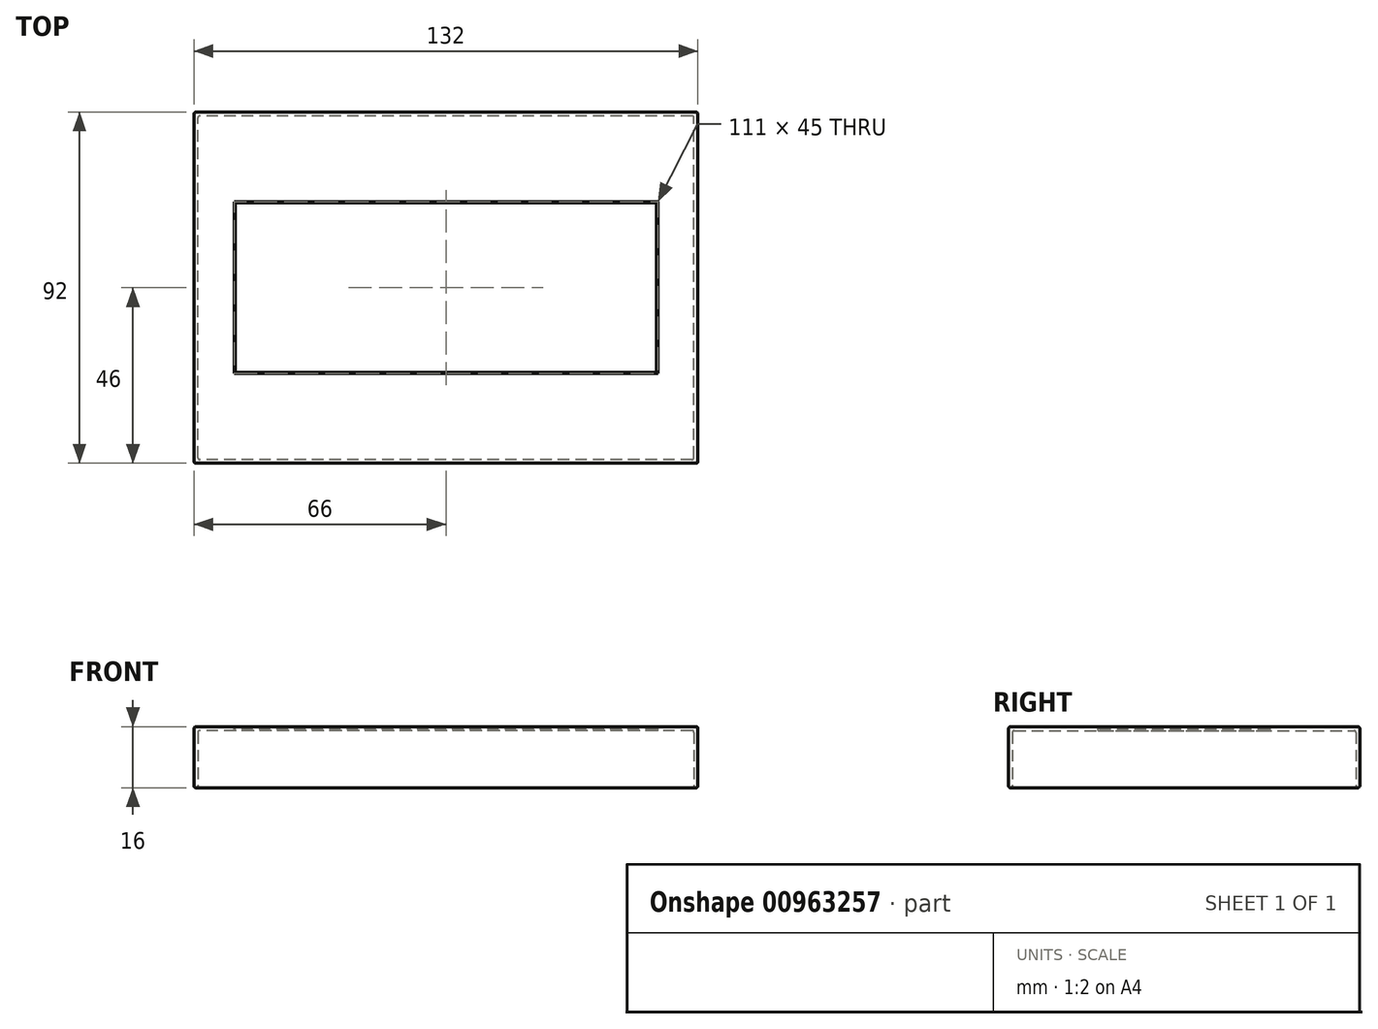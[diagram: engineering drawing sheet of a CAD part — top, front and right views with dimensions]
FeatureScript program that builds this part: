
annotation { "Feature Type Name" : "Feature", "Feature Type Description" : "" }
export const myFeature = defineFeature(function(context is Context, id is Id, definition is map)
    precondition{}
    {
        {
            var Q0;
            Q0=qCreatedBy(makeId("Top.planeOp"),FACE);
            var sketch = newSketch(context, id + "F0", { "sketchPlane" : qUnion([Q0])});
            skLineSegment(sketch, "E0.bottom", {"start": v(66, -46) * mm, "end": v(-66, -46) * mm});
            skLineSegment(sketch, "E0.top", {"start": v(66, 46) * mm, "end": v(-66, 46) * mm});
            skLineSegment(sketch, "E0.left", {"start": v(66, -46) * mm, "end": v(66, 46) * mm});
            skLineSegment(sketch, "E0.right", {"start": v(-66, -46) * mm, "end": v(-66, 46) * mm});
            skPoint(sketch, "E0.middle", {"position": v(0, 0) * mm});
            skSolve(sketch);
        }
        {
            var Q0;
            Q0 = qSketchRegion(id + "F0", true);
            extrude(context, id + "F1", {"entities" : qUnion([Q0]), "depth" : 16 * mm, "offsetDistance" : 25 * mm});
        }
        {
            var Q0;
            Q0=makeQuery(id+"F1.opExtrude","CAP_FACE",FACE,{"disambiguationData":[OSD([sQuery(id+"F0.wireOp",EDGE,"E0.bottom"),sQuery(id+"F0.wireOp",EDGE,"E0.top"),sQuery(id+"F0.wireOp",EDGE,"E0.left"),sQuery(id+"F0.wireOp",EDGE,"E0.right")])],"isStart":true});
            shell(context, id + "F2", {"entities" : qUnion([Q0]), "thickness" : 1 * mm});
        }
        {
            var Q0;
            Q0=makeQuery(id+"F1.opExtrude","SWEPT_EDGE",EDGE,{"disambiguationData":[OSD([sQuery(id+"F0.wireOp",EDGE,"E0.bottom"),sQuery(id+"F0.wireOp",EDGE,"E0.left")])]});
            var Q1;
            Q1=makeQuery(id+"F1.opExtrude","SWEPT_FACE",FACE,{"disambiguationData":[OSD([sQuery(id+"F0.wireOp",EDGE,"E0.bottom")])]});
            var Q2;
            Q2=makeQuery(id+"F1.opExtrude","SWEPT_EDGE",EDGE,{"disambiguationData":[OSD([sQuery(id+"F0.wireOp",EDGE,"E0.bottom"),sQuery(id+"F0.wireOp",EDGE,"E0.right")])]});
            var Q3;
            Q3=makeQuery(id+"F1.opExtrude","SWEPT_EDGE",EDGE,{"disambiguationData":[OSD([sQuery(id+"F0.wireOp",EDGE,"E0.top"),sQuery(id+"F0.wireOp",EDGE,"E0.left")])]});
            var Q4;
            Q4=makeQuery(id+"F1.opExtrude","CAP_FACE",FACE,{"disambiguationData":[OSD([sQuery(id+"F0.wireOp",EDGE,"E0.bottom"),sQuery(id+"F0.wireOp",EDGE,"E0.top"),sQuery(id+"F0.wireOp",EDGE,"E0.left"),sQuery(id+"F0.wireOp",EDGE,"E0.right")])],"isStart":false});
            var Q5;
            Q5=makeQuery(id+"F1.opExtrude","SWEPT_EDGE",EDGE,{"disambiguationData":[OSD([sQuery(id+"F0.wireOp",EDGE,"E0.top"),sQuery(id+"F0.wireOp",EDGE,"E0.right")])]});
            var Q6;
            Q6=makeQuery(id+"F1.opExtrude","SWEPT_FACE",FACE,{"disambiguationData":[OSD([sQuery(id+"F0.wireOp",EDGE,"E0.top")])]});
            var Q7;
            Q7=makeQuery(id+"F1.opExtrude","CAP_EDGE",EDGE,{"disambiguationData":[OSD([sQuery(id+"F0.wireOp",EDGE,"E0.bottom")])],"isStart":true});
            var Q8;
            Q8=makeQuery(id+"F1.opExtrude","SWEPT_FACE",FACE,{"disambiguationData":[OSD([sQuery(id+"F0.wireOp",EDGE,"E0.left")])]});
            var Q9;
            Q9=makeQuery(id+"F1.opExtrude","CAP_EDGE",EDGE,{"disambiguationData":[OSD([sQuery(id+"F0.wireOp",EDGE,"E0.bottom")])],"isStart":false});
            var Q10;
            Q10=makeQuery(id+"F1.opExtrude","SWEPT_FACE",FACE,{"disambiguationData":[OSD([sQuery(id+"F0.wireOp",EDGE,"E0.right")])]});
            var Q11;
            Q11=makeQuery(id+"F1.opExtrude","CAP_EDGE",EDGE,{"disambiguationData":[OSD([sQuery(id+"F0.wireOp",EDGE,"E0.top")])],"isStart":true});
            var Q12;
            Q12=makeQuery(id+"F1.opExtrude","CAP_EDGE",EDGE,{"disambiguationData":[OSD([sQuery(id+"F0.wireOp",EDGE,"E0.left")])],"isStart":true});
            var Q13;
            Q13=makeQuery(id+"F1.opExtrude","CAP_EDGE",EDGE,{"disambiguationData":[OSD([sQuery(id+"F0.wireOp",EDGE,"E0.right")])],"isStart":true});
            var Q14;
            Q14=makeQuery(id+"F1.opExtrude","CAP_EDGE",EDGE,{"disambiguationData":[OSD([sQuery(id+"F0.wireOp",EDGE,"E0.right")])],"isStart":false});
            var Q15;
            Q15=makeQuery(id+"F2.opShell","OFFSET_FACE",FACE,{"disambiguationData":[OSD([sQuery(id+"F0.wireOp",EDGE,"E0.bottom")])]});
            var Q16;
            Q16=makeQuery(id+"F2.opShell","OFFSET_FACE",FACE,{"disambiguationData":[OSD([sQuery(id+"F0.wireOp",EDGE,"E0.bottom"),sQuery(id+"F0.wireOp",EDGE,"E0.top"),sQuery(id+"F0.wireOp",EDGE,"E0.left"),sQuery(id+"F0.wireOp",EDGE,"E0.right")])]});
            var Q17;
            Q17=makeQuery(id+"F2.opShell","OFFSET_EDGE",EDGE,{"disambiguationData":[OSD([sQuery(id+"F0.wireOp",EDGE,"E0.top"),sQuery(id+"F0.wireOp",EDGE,"E0.left")])]});
            var Q18;
            Q18=makeQuery(id+"F2.opShell","OFFSET_FACE",FACE,{"disambiguationData":[OSD([sQuery(id+"F0.wireOp",EDGE,"E0.top")])]});
            var Q19;
            Q19=makeQuery(id+"F2.opShell","OFFSET_EDGE",EDGE,{"disambiguationData":[OSD([sQuery(id+"F0.wireOp",EDGE,"E0.top"),sQuery(id+"F0.wireOp",EDGE,"E0.right")])]});
            var Q20;
            Q20=makeQuery(id+"F2.opShell","OFFSET_FACE",FACE,{"disambiguationData":[OSD([sQuery(id+"F0.wireOp",EDGE,"E0.left")])]});
            var Q21;
            {var subQ0=sQuery(id+"F0.wireOp",EDGE,"E0.bottom");Q21=makeQuery(id+"F2.opShell","OFFSET_EDGE",EDGE,{"disambiguationData":[OSD([subQ0]),TDD([makeQuery(id+"F1.opExtrude","CAP_EDGE",EDGE,{"disambiguationData":[OSD([subQ0])],"isStart":true})])]});}
            var Q22;
            Q22=makeQuery(id+"F2.opShell","OFFSET_FACE",FACE,{"disambiguationData":[OSD([sQuery(id+"F0.wireOp",EDGE,"E0.right")])]});
            var Q23;
            Q23=makeQuery(id+"F1.opExtrude","CAP_FACE",FACE,{"disambiguationData":[OSD([sQuery(id+"F0.wireOp",EDGE,"E0.bottom"),sQuery(id+"F0.wireOp",EDGE,"E0.top"),sQuery(id+"F0.wireOp",EDGE,"E0.left"),sQuery(id+"F0.wireOp",EDGE,"E0.right")])],"isStart":true});
            var Q24;
            {var subQ0=sQuery(id+"F0.wireOp",EDGE,"E0.top");Q24=makeQuery(id+"F2.opShell","OFFSET_EDGE",EDGE,{"disambiguationData":[OSD([subQ0]),TDD([makeQuery(id+"F1.opExtrude","CAP_EDGE",EDGE,{"disambiguationData":[OSD([subQ0])],"isStart":true})])]});}
            var Q25;
            {var subQ0=sQuery(id+"F0.wireOp",EDGE,"E0.top");Q25=makeQuery(id+"F2.opShell","OFFSET_EDGE",EDGE,{"disambiguationData":[OSD([subQ0]),TDD([makeQuery(id+"F1.opExtrude","CAP_EDGE",EDGE,{"disambiguationData":[OSD([subQ0])],"isStart":false})])]});}
            var Q26;
            {var subQ0=sQuery(id+"F0.wireOp",EDGE,"E0.left");Q26=makeQuery(id+"F2.opShell","OFFSET_EDGE",EDGE,{"disambiguationData":[OSD([subQ0]),TDD([makeQuery(id+"F1.opExtrude","CAP_EDGE",EDGE,{"disambiguationData":[OSD([subQ0])],"isStart":true})])]});}
            var Q27;
            {var subQ0=sQuery(id+"F0.wireOp",EDGE,"E0.left");Q27=makeQuery(id+"F2.opShell","OFFSET_EDGE",EDGE,{"disambiguationData":[OSD([subQ0]),TDD([makeQuery(id+"F1.opExtrude","CAP_EDGE",EDGE,{"disambiguationData":[OSD([subQ0])],"isStart":false})])]});}
            var Q28;
            {var subQ0=sQuery(id+"F0.wireOp",EDGE,"E0.right");Q28=makeQuery(id+"F2.opShell","OFFSET_EDGE",EDGE,{"disambiguationData":[OSD([subQ0]),TDD([makeQuery(id+"F1.opExtrude","CAP_EDGE",EDGE,{"disambiguationData":[OSD([subQ0])],"isStart":true})])]});}
            var Q29;
            Q29=makeQuery(id+"F1.opExtrude","CAP_EDGE",EDGE,{"disambiguationData":[OSD([sQuery(id+"F0.wireOp",EDGE,"E0.top")])],"isStart":false});
            var Q30;
            Q30=makeQuery(id+"F1.opExtrude","CAP_EDGE",EDGE,{"disambiguationData":[OSD([sQuery(id+"F0.wireOp",EDGE,"E0.left")])],"isStart":false});
            var Q31;
            Q31=makeQuery(id+"F2.opShell","OFFSET_EDGE",EDGE,{"disambiguationData":[OSD([sQuery(id+"F0.wireOp",EDGE,"E0.bottom"),sQuery(id+"F0.wireOp",EDGE,"E0.left")])]});
            var Q32;
            Q32=makeQuery(id+"F2.opShell","OFFSET_EDGE",EDGE,{"disambiguationData":[OSD([sQuery(id+"F0.wireOp",EDGE,"E0.bottom"),sQuery(id+"F0.wireOp",EDGE,"E0.right")])]});
            var Q33;
            {var subQ0=sQuery(id+"F0.wireOp",EDGE,"E0.bottom");Q33=makeQuery(id+"F2.opShell","OFFSET_EDGE",EDGE,{"disambiguationData":[OSD([subQ0]),TDD([makeQuery(id+"F1.opExtrude","CAP_EDGE",EDGE,{"disambiguationData":[OSD([subQ0])],"isStart":false})])]});}
            var Q34;
            {var subQ0=sQuery(id+"F0.wireOp",EDGE,"E0.right");Q34=makeQuery(id+"F2.opShell","OFFSET_EDGE",EDGE,{"disambiguationData":[OSD([subQ0]),TDD([makeQuery(id+"F1.opExtrude","CAP_EDGE",EDGE,{"disambiguationData":[OSD([subQ0])],"isStart":false})])]});}
            fillet(context, id + "F3", {"entities" : qUnion([Q0, Q1, Q2, Q3, Q4, Q5, Q6, Q7, Q8, Q9, Q10, Q11, Q12, Q13, Q14, Q15, Q16, Q17, Q18, Q19, Q20, Q21, Q22, Q23, Q24, Q25, Q26, Q27, Q28, Q29, Q30, Q31, Q32, Q33, Q34]), "radius" : 0.5 * mm, "tangentPropagation" : true, "allowEdgeOverflow" : false});
        }
        {
            var Q0;
            Q0=makeQuery(id+"F1.opExtrude","CAP_FACE",FACE,{"disambiguationData":[OSD([sQuery(id+"F0.wireOp",EDGE,"E0.bottom"),sQuery(id+"F0.wireOp",EDGE,"E0.top"),sQuery(id+"F0.wireOp",EDGE,"E0.left"),sQuery(id+"F0.wireOp",EDGE,"E0.right")])],"isStart":false});
            var sketch = newSketch(context, id + "F4", { "sketchPlane" : qUnion([Q0])});
            skLineSegment(sketch, "E1.bottom", {"start": v(55.5, -22.5) * mm, "end": v(-55.5, -22.5) * mm});
            skLineSegment(sketch, "E1.top", {"start": v(55.5, 22.5) * mm, "end": v(-55.5, 22.5) * mm});
            skLineSegment(sketch, "E1.left", {"start": v(55.5, -22.5) * mm, "end": v(55.5, 22.5) * mm});
            skLineSegment(sketch, "E1.right", {"start": v(-55.5, -22.5) * mm, "end": v(-55.5, 22.5) * mm});
            skPoint(sketch, "E1.middle", {"position": v(0, 0) * mm});
            skSolve(sketch);
        }
        {
            var Q0;
            Q0 = qSketchRegion(id + "F4", true);
            extrude(context, id + "F5", {"entities" : qUnion([Q0]), "operationType" : NewBodyOperationType.REMOVE, "oppositeDirection" : true, "depth" : 2 * mm, "offsetDistance" : 25 * mm});
        }
        {
            var Q0;
            Q0=makeQuery(id+"F1.opExtrude","CAP_FACE",FACE,{"disambiguationData":[OSD([sQuery(id+"F0.wireOp",EDGE,"E0.bottom"),sQuery(id+"F0.wireOp",EDGE,"E0.top"),sQuery(id+"F0.wireOp",EDGE,"E0.left"),sQuery(id+"F0.wireOp",EDGE,"E0.right")])],"isStart":false});
            var sketch = newSketch(context, id + "F6", { "sketchPlane" : qUnion([Q0])});
            skLineSegment(sketch, "E2.0", {"start": v(55.2, 22.2) * mm, "end": v(-55.2, 22.2) * mm});
            skLineSegment(sketch, "E2.1", {"start": v(55.2, -22.2) * mm, "end": v(55.2, 22.2) * mm});
            skLineSegment(sketch, "E2.2", {"start": v(55.2, -22.2) * mm, "end": v(-55.2, -22.2) * mm});
            skLineSegment(sketch, "E2.3", {"start": v(-55.2, -22.2) * mm, "end": v(-55.2, 22.2) * mm});
            skSolve(sketch);
        }
        {
            var Q0;
            Q0 = qSketchRegion(id + "F6", true);
            extrude(context, id + "F7", {"entities" : qUnion([Q0]), "oppositeDirection" : true, "depth" : 0.6 * mm, "offsetDistance" : 25 * mm});
        }
    });
